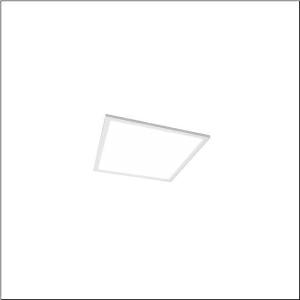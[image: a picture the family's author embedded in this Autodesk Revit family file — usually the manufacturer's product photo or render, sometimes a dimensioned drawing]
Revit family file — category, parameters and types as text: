
# Revit family: apollon_r__21_square_51mq13wd2414_6bd0
name_source: partatom
category: Lighting Fixtures
units: mm (PartAtom-declared; Revit-internal decimal feet)

## family parameters
Cut with Voids When Loaded = No
Host = Face
Light Source = No
Part Type = Normal
Room Calculation Point = No
Round Connector Dimension = Use Diameter
Shared = No

## types (1)
- Apollon® 21 square (1 x LED, 1800 lm, 14 W, 4000K)
    Apparent Load = 14 VA
    CIE Flux Codes = 68 89 97 100 100
    Color Rendering = 80
    Color Temperature = 4000K
    Default Elevation = 1800 mm  [stored 5.90551 ft]
    Description = Apollon® 21 square, office luminaire, primary optical cover: micro prismatic cover, of PMMA, CAT 2 (L<= 3000cd/m²), light emission: direct distribution, primary light characteristic: symmetric, installation type: lay-in mounting, LED, rated luminous flux: 1.800lm, luminous efficacy: 129lm/W, light colour: 840, colour temperature: 4000K, with terminal, 5-pole, mains connection: 220..240V, AC/DC, 0/50..60Hz, rated input power: 14W, housing, of sheet steel, coated, traffic white (RAL 9016), length: 296mm, width: 296mm, height: 30mm, housing upper side, of sheet steel, galvanised, protection rating (complete): IP20, protection rating (lamp compartment, on room side): IP50, insulation class (complete): insulation class II (safety insulation), certification: CE, ENEC, impact resistance: IK03, permissible operating ambient temperature: -20..+45°C, permissible storage temperature: -40..+80°C, packaging unit: 1 piece
    Height = 0 mm  [stored 0 ft]
    Lamp = 1 x LED
    Lamp Light Flux = 1800 lm
    Lamp Power = 14 W
    Lamp count = 1
    Length = 295 mm
    Luminous efficacy = 129 lm/W
    Manufacturer = Siteco
    ModVariant = No
    Model = 51MQ13WD2414
    Mounting Place = Ceiling
    Mounting Type = Recessed
    Number of Poles = 1
    OnlyDefault = Yes
    Power Factor = 1
    Product Name = Apollon® 21 square
    Product group = office luminaire | ceiling recessed
    ProductGroupID = 401
    Protection Class = Protection class II
    Protection Degree = IP 20
    RLX_Detail_Level = 1
    RLX_Emergency_Light_Flux = 0 lm
    RLX_Emergency_Type = 0
    RLX_Emergency_Type_DB = No
    RlxData = <blob elided: 9253 chars, md5=3767088f>
    Socket = socket
    Standby Power = 0 W
    System Light Flux = 1800 lm
    System Power = 14 W
    Type Comments = Product without accessories
    Type Image = l_1291030.jpg
    URL = http://relux.com
    VarID = ---
    Voltage = 0 V
    Weight = 0.00 kg
    Width = 295 mm

note: [stored X ft] marks values corroborated as IEEE doubles in the binary element streams (Revit-internal decimal feet)

## geometry (parser evidence)
native form markers: Sweep x10
no freeform markers — native parametric forms only
